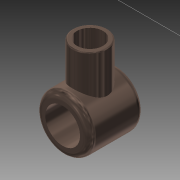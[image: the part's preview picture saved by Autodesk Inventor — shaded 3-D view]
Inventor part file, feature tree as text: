
AUTODESK INVENTOR PART (.ipt)
format: ipt  version: 2015 (Build 190159000, 159)  size: 136,192 bytes
history: native  units: mm
features: extrude x3, sketch x3, fillet x2, hole x1
ambient origin geometry x8: Origin, YZ Plane, XZ Plane, XY Plane, X Axis, Y Axis, Z Axis, Center Point
bodies: Solid1 (feature_tree)
feature tree (9):
  extrude  "Extrusion1"  Depth=40.0mm
  fillet  "Fillet2"  Radius=40.0mm
  extrude  "Extrusion6"  Depth=25.4mm
  extrude  "Extrusion7"  Depth=1.0mm TaperAngle=0.0deg
  hole  "Hole2"  [1 undecoded]
  fillet  "Fillet3"  Radius=1.0mm
  sketch  "Sketch1"  dims[d0=25.4mm d1=40.0mm d6=40.0mm d7=0.0mm]
  sketch  "Sketch6"  dims[d32=5.0mm d33=25.4mm]
  sketch  "Sketch7"  dims[d34=65.4mm d35=0.0mm d36=40.0mm d37=0.0mm d38=10.0mm d39=10.0mm d40=19.0mm d41=6.0mm d42=4.0mm d43=2.0mm d44=90.0deg d45=15.0mm d46=0.0mm d47=1.0mm]
note: 1 required parameter value undecoded (feature->parameter linkage not recoverable at this tier; creation-order binding heuristic only, values carry confidence <= 0.55)
